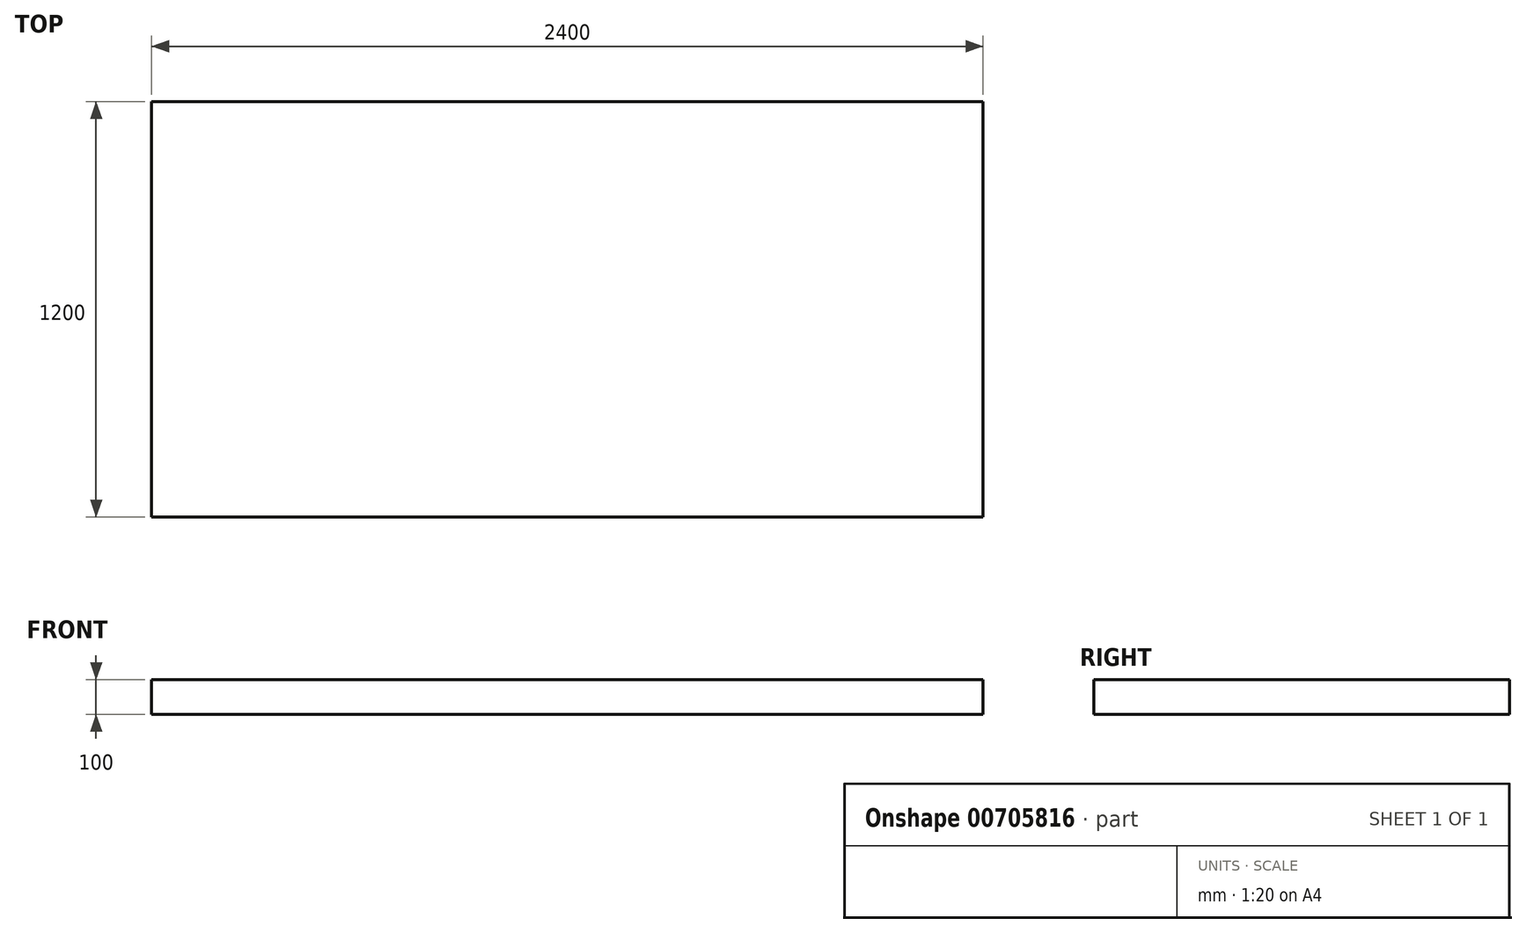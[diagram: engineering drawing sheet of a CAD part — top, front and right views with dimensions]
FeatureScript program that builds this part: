
annotation { "Feature Type Name" : "Feature", "Feature Type Description" : "" }
export const myFeature = defineFeature(function(context is Context, id is Id, definition is map)
    precondition{}
    {
        {
            var Q0;
            Q0=qCreatedBy(makeId("Top.planeOp"),FACE);
            var sketch = newSketch(context, id + "F0", { "sketchPlane" : qUnion([Q0])});
            skLineSegment(sketch, "E0.bottom", {"start": v(-112.41, -34.53) * mm, "end": v(2287.59, -34.53) * mm});
            skLineSegment(sketch, "E0.top", {"start": v(-112.41, 1165.47) * mm, "end": v(2287.59, 1165.47) * mm});
            skLineSegment(sketch, "E0.left", {"start": v(-112.41, -34.53) * mm, "end": v(-112.41, 1165.47) * mm});
            skLineSegment(sketch, "E0.right", {"start": v(2287.59, -34.53) * mm, "end": v(2287.59, 1165.47) * mm});
            skSolve(sketch);
        }
        {
            var Q0;
            Q0=makeQuery(id+"F0.imprint","IMPRINT",FACE,{"disambiguationData":[TD([[makeQuery(id+"F0.imprint","IMPRINT",EDGE,{"derivedFrom":sQuery(id+"F0.wireOp",EDGE,"E0.bottom")}),1.0]])]});
            extrude(context, id + "F1", {"entities" : qUnion([Q0]), "depth" : 100 * mm, "offsetDistance" : 25 * mm});
        }
    });
